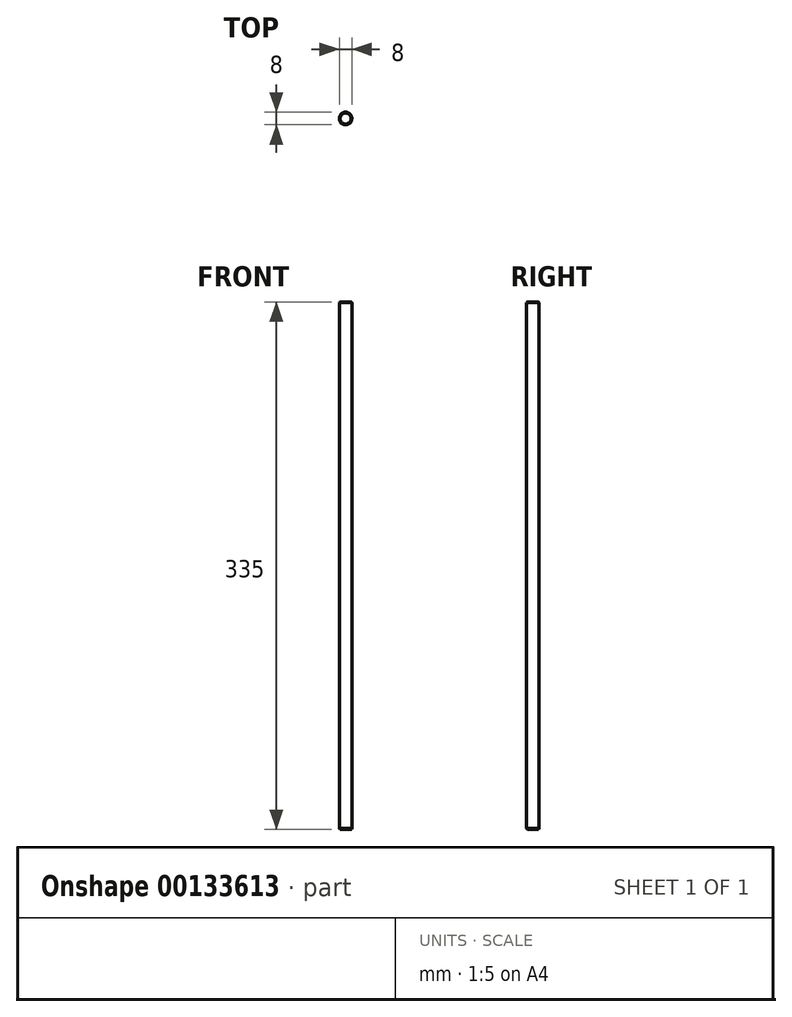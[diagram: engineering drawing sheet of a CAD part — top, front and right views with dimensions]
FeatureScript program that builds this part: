
annotation { "Feature Type Name" : "Feature", "Feature Type Description" : "" }
export const myFeature = defineFeature(function(context is Context, id is Id, definition is map)
    precondition{}
    {
        {
            var Q0;
            Q0=qCreatedBy(makeId("Top.planeOp"),FACE);
            var sketch = newSketch(context, id + "F0", { "sketchPlane" : qUnion([Q0])});
            skCircle(sketch, "E0", {"center": v(0, 0) * mm, "radius": 4 * mm});
            skSolve(sketch);
        }
        {
            var Q0;
            Q0=makeQuery(id+"F0.imprint","IMPRINT",FACE,{"disambiguationData":[TD([[makeQuery(id+"F0.imprint","IMPRINT",EDGE,{"derivedFrom":sQuery(id+"F0.wireOp",EDGE,"E0")}),1.0]])]});
            extrude(context, id + "F1", {"entities" : qUnion([Q0]), "depth" : 335 * mm});
        }
        {
            var Q0;
            Q0=makeQuery(id+"F1.opExtrude","CAP_EDGE",EDGE,{"disambiguationData":[OSD([sQuery(id+"F0.wireOp",EDGE,"E0")])],"isStart":false});
            var Q1;
            Q1=makeQuery(id+"F1.opExtrude","CAP_EDGE",EDGE,{"disambiguationData":[OSD([sQuery(id+"F0.wireOp",EDGE,"E0")])],"isStart":true});
            chamfer(context, id + "F2", {"entities" : qUnion([Q0, Q1]), "width" : 0.5 * mm});
        }
    });
